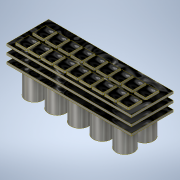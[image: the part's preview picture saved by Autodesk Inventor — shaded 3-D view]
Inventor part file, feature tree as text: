
AUTODESK INVENTOR PART (.ipt)
format: ipt  version: 2020 (Build 240168000, 168)  size: 667,648 bytes
history: native  units: mm
features: chamfer x16, extrude x9, sketch x9, other x2
ambient origin geometry x8: Origin, YZ Plane, XZ Plane, XY Plane, X Axis, Y Axis, Z Axis, Center Point
bodies: Body1 (feature_tree)
feature tree (36):
  other  "Bryła1"
  extrude  "Wyciągnięcie proste1"  Depth=18.73mm
  extrude  "Wyciągnięcie proste2"  Depth=9.365mm
  chamfer  "Faza1"  Distance=55.88mm
  chamfer  "Faza2"  Distance=27.94mm
  chamfer  "Faza3"  Distance=1.0mm
  extrude  "Wyciągnięcie proste3"  Depth=6.03mm
  chamfer  "Faza4"  Distance=5.08mm
  extrude  "Wyciągnięcie proste4"  Depth=2.54mm
  chamfer  "Faza5"  Distance=1.27mm
  chamfer  "Faza6"  Distance=5.08mm
  chamfer  "Faza7"  Distance=6.03mm
  chamfer  "Faza8"  Distance=1.27mm
  chamfer  "Faza9"  Distance=0.64mm
  chamfer  "Faza10"  Distance=5.08mm
  chamfer  "Faza11"  Distance=0.64mm
  chamfer  "Faza12"  Distance=5.08mm
  chamfer  "Faza13"  Distance=0.64mm
  chamfer  "Faza14"  Distance=5.08mm
  chamfer  "Faza15"  Distance=0.64mm
  chamfer  "Faza16"  Distance=5.08mm
  other  "Płaszczyzna konstrukcyjna1"
  extrude  "Wyciągnięcie proste5"  Depth=5.08mm
  extrude  "Wyciągnięcie proste6"  Depth=5.08mm
  extrude  "Wyciągnięcie proste7"  Depth=5.08mm
  extrude  "Wyciągnięcie proste8"  Depth=0.64mm
  extrude  "Wyciągnięcie proste9"  Depth=0.64mm
  sketch  "Szkic1"
  sketch  "Szkic2"
  sketch  "Szkic3"
  sketch  "Szkic4"
  sketch  "Szkic5"
  sketch  "Szkic6"
  sketch  "Szkic7"
  sketch  "Szkic8"
  sketch  "Szkic9"
